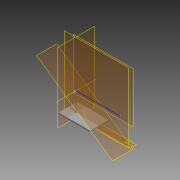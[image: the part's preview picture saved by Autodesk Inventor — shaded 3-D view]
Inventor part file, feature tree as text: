
AUTODESK INVENTOR PART (.ipt)
format: ipt  version: 2012 SP2 (Build 160219200, 219)  size: 241,664 bytes
history: native  units: in
note: dims shown in document units (in); Inventor stores cm internally (conversion verified against a paired STEP export)
features: sketch x11, extrude x8, plane x6, other x2, loft x1, fillet x1, projected_geometry x1
ambient origin geometry x8: Origin, YZ Plane, XZ Plane, XY Plane, X Axis, Y Axis, Z Axis, Center Point
bodies: Solid1 (feature_tree)
feature tree (30):
  sketch  "Sketch1"  dims[d0=3.5433in d1=3.937in]
  plane  "Work Plane1"
  extrude  "Extrusion1"  Depth=3.937in
  extrude  "Extrusion2"  Depth=9.8425in
  extrude  "Extrusion3"  Depth=0.7874in
  plane  "Work Plane2"
  sketch  "Sketch5"  dims[d10=25.9562in d11=0.0in d12=0.5906in]
  plane  "Work Plane3"
  extrude  "Extrusion4"  Depth=0.1575in
  extrude  "Extrusion5"  Depth=0.5906in
  plane  "Work Plane4"
  extrude  "Extrusion6"  Depth=0.315in
  plane  "Work Plane5"
  loft  "Loft1"
  plane  "Work Plane6"
  extrude  "Extrusion7"  Depth=0.3937in TaperAngle=0.0deg
  fillet  "Fillet1"  Radius=0.1575in
  extrude  "Extrusion8"  TaperAngle=0.0deg  [1 undecoded]
  sketch  "Sketch2"  dims[d2=3.937in d3=9.8425in]
  sketch  "Sketch3"  dims[d4=0.5906in d5=0.0in d6=0.7874in]
  sketch  "Sketch4"  dims[d7=0.3937in d8=0.0in d9=0.1575in]
  sketch  "Sketch6"  dims[d13=0.5906in d14=0.315in d15=0.315in d16=-0.1374in d17=-0.1374in]
  sketch  "Sketch7"  dims[d18=0.1575in d19=18.69in d20=0.0in]
  sketch  "Sketch8"  dims[d21=0.1575in d22=0.3937in d23=0.0in d24=0.1575in]
  sketch  "Sketch9"  dims[d25=0.0197in d27=0.0in d28=90.0deg]
  other  "Edges1"
  other  "Work Axis1"
  sketch  "Sketch10"  dims[d29=0.3937in d30=90.0deg]
  projected_geometry  "Projected Loop1"
  sketch  "Sketch11"  dims[d31=0.2405in d33=0.3937in d34=0.315in d36=0.1575in d37=0.1374in d38=0.0787in d39=0.1181in d40=0.0in d41=0.0394in d42=1.378in d43=1.378in d44=0.2431in d45=0.0in]
note: 1 required parameter value undecoded (feature->parameter linkage not recoverable at this tier; creation-order binding heuristic only, values carry confidence <= 0.55)
